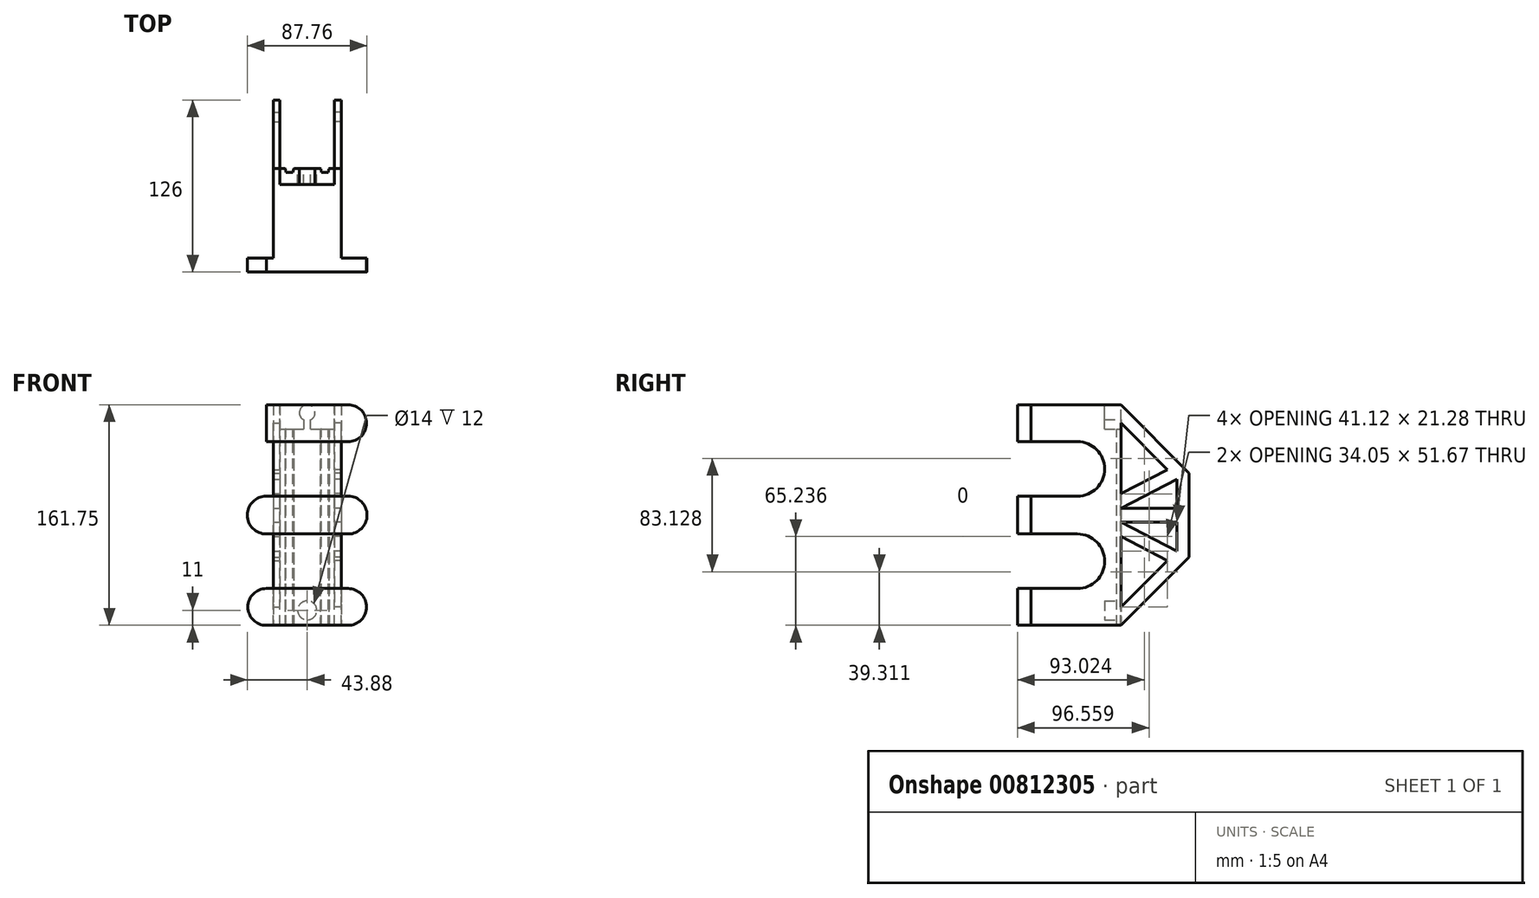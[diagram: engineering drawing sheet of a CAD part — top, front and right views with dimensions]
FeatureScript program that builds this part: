
annotation { "Feature Type Name" : "Feature", "Feature Type Description" : "" }
export const myFeature = defineFeature(function(context is Context, id is Id, definition is map)
    precondition{}
    {
        {
            var Q0;
            Q0=qCreatedBy(makeId("Top.planeOp"),FACE);
            var sketch = newSketch(context, id + "F0", { "sketchPlane" : qUnion([Q0])});
            skLineSegment(sketch, "E0.bottom", {"start": v(-20, 6) * mm, "end": v(20, 6) * mm});
            skLineSegment(sketch, "E0.top", {"start": v(-20, -6) * mm, "end": v(20, -6) * mm});
            skLineSegment(sketch, "E0.left", {"start": v(-20, 6) * mm, "end": v(-20, -6) * mm});
            skLineSegment(sketch, "E0.right", {"start": v(20, 6) * mm, "end": v(20, -6) * mm});
            skLineSegment(sketch, "E1", {"start": v(10.53, 3) * mm, "end": v(15.53, 3) * mm});
            skLineSegment(sketch, "E2", {"start": v(-15.53, 3) * mm, "end": v(-10.53, 3) * mm});
            skLineSegment(sketch, "E3", {"start": v(-20, 6) * mm, "end": v(20, -6) * mm, "construction": true});
            skLineSegment(sketch, "E4", {"start": v(-10.53, 3) * mm, "end": v(-10, 6) * mm});
            skLineSegment(sketch, "E5", {"start": v(-15.53, 3) * mm, "end": v(-16, 6) * mm});
            skLineSegment(sketch, "E6", {"start": v(10.53, 3) * mm, "end": v(10, 6) * mm});
            skLineSegment(sketch, "E7", {"start": v(15.53, 3) * mm, "end": v(16, 6) * mm});
            skSolve(sketch);
        }
        {
            var Q0;
            Q0=qCreatedBy(makeId("Front.planeOp"),FACE);
            var sketch = newSketch(context, id + "F1", { "sketchPlane" : qUnion([Q0])});
            skLineSegment(sketch, "E8", {"start": v(0, 144) * mm, "end": v(0, 0) * mm});
            skSolve(sketch);
        }
        {
            var Q0;
            Q0=makeQuery(id+"F0.imprint","IMPRINT",FACE,{"disambiguationData":[TD([[makeQuery(id+"F0.imprint","IMPRINT",EDGE,{"derivedFrom":sQuery(id+"F0.wireOp",EDGE,"E0.top")}),1.0]])]});
            var Q1;
            Q1=sQuery(id+"F1.wireOp",EDGE,"E8");
            sweep(context, id + "F2", {"profiles" : qUnion([Q0]), "path" : qUnion([Q1])});
        }
        {
            var Q0;
            Q0=makeQuery(id+"F2.opSweep","SWEPT_EDGE",EDGE,{"disambiguationData":[OSD([sQuery(id+"F0.wireOp",EDGE,"E0.bottom"),sQuery(id+"F0.wireOp",EDGE,"E4"),sQuery(id+"F1.wireOp",EDGE,"E8")])]});
            var Q1;
            Q1=makeQuery(id+"F2.opSweep","SWEPT_EDGE",EDGE,{"disambiguationData":[OSD([sQuery(id+"F0.wireOp",EDGE,"E0.bottom"),sQuery(id+"F0.wireOp",EDGE,"E5"),sQuery(id+"F1.wireOp",EDGE,"E8")])]});
            var Q2;
            Q2=makeQuery(id+"F2.opSweep","SWEPT_EDGE",EDGE,{"disambiguationData":[OSD([sQuery(id+"F0.wireOp",EDGE,"E0.bottom"),sQuery(id+"F0.wireOp",EDGE,"E6"),sQuery(id+"F1.wireOp",EDGE,"E8")])]});
            var Q3;
            Q3=makeQuery(id+"F2.opSweep","SWEPT_EDGE",EDGE,{"disambiguationData":[OSD([sQuery(id+"F0.wireOp",EDGE,"E0.bottom"),sQuery(id+"F0.wireOp",EDGE,"E7"),sQuery(id+"F1.wireOp",EDGE,"E8")])]});
            chamfer(context, id + "F3", {"entities" : qUnion([Q0, Q1, Q2, Q3]), "width" : 0.5 * mm, "tangentPropagation" : true});
        }
        {
            var Q0;
            Q0=qCreatedBy(makeId("Front.planeOp"),FACE);
            var sketch = newSketch(context, id + "F4", { "sketchPlane" : qUnion([Q0])});
            skLineSegment(sketch, "E9.0", {"start": v(9.5, 144) * mm, "end": v(-9.5, 144) * mm});
            skLineSegment(sketch, "E10", {"start": v(2.5, 144) * mm, "end": v(2.5, 151) * mm});
            skLineSegment(sketch, "E11", {"start": v(2.5, 151) * mm, "end": v(-2.5, 151) * mm});
            skLineSegment(sketch, "E12", {"start": v(-2.5, 151) * mm, "end": v(-2.5, 144) * mm});
            skLineSegment(sketch, "E13", {"start": v(2.5, 144) * mm, "end": v(9.5, 144) * mm, "construction": true});
            skLineSegment(sketch, "E14", {"start": v(-2.5, 144) * mm, "end": v(-9.5, 144) * mm, "construction": true});
            skPoint(sketch, "E15", {"position": v(0, 156) * mm});
            skCircle(sketch, "E16", {"center": v(0, 156) * mm, "radius": 5.75 * mm});
            skLineSegment(sketch, "E17", {"start": v(0, 144) * mm, "end": v(0, 168) * mm});
            skSolve(sketch);
        }
        {
            var Q0;
            Q0=qCreatedBy(makeId("Front.planeOp"),FACE);
            var sketch = newSketch(context, id + "F5", { "sketchPlane" : qUnion([Q0])});
            skLineSegment(sketch, "E18.0", {"start": v(9.5, 0) * mm, "end": v(-9.5, 0) * mm});
            skLineSegment(sketch, "E19.bottom", {"start": v(3.5, 0) * mm, "end": v(-3.5, 0) * mm});
            skLineSegment(sketch, "E19.top", {"start": v(3.5, 5) * mm, "end": v(-3.5, 5) * mm});
            skLineSegment(sketch, "E19.left", {"start": v(3.5, 0) * mm, "end": v(3.5, 5) * mm});
            skLineSegment(sketch, "E19.right", {"start": v(-3.5, 0) * mm, "end": v(-3.5, 5) * mm});
            skLineSegment(sketch, "E20", {"start": v(9.5, 0) * mm, "end": v(3.5, 0) * mm, "construction": true});
            skLineSegment(sketch, "E21", {"start": v(-3.5, 0) * mm, "end": v(-9.5, 0) * mm, "construction": true});
            skCircle(sketch, "E22", {"center": v(0, 11) * mm, "radius": 7 * mm});
            skPoint(sketch, "E22.centerSnap0", {"position": v(0, 5) * mm});
            skSolve(sketch);
        }
        {
            var Q0;
            {var subQ0=sQuery(id+"F1.wireOp",EDGE,"E8");var subQ1=sQuery(id+"F0.wireOp",EDGE,"E0.bottom");Q0=makeQuery(id+"F2.opSweep","SWEPT_FACE",FACE,{"disambiguationData":[OSD([subQ1,subQ0]),TDD([makeQuery(id+"F0.imprint","IMPRINT",EDGE,{"disambiguationData":[TD([[makeQuery(id+"F0.imprint","INTERSECT",VERTEX,{"derivedFrom":[subQ1,sQuery(id+"F0.wireOp",EDGE,"E4")]}),-1.0]])],"derivedFrom":subQ1}),subQ0])]});}
            var sketch = newSketch(context, id + "F6", { "sketchPlane" : qUnion([Q0])});
            skCircle(sketch, "E23.0", {"center": v(0, 11) * mm, "radius": 7 * mm});
            skLineSegment(sketch, "E24.0", {"start": v(3.5, 0) * mm, "end": v(3.5, 5) * mm});
            skLineSegment(sketch, "E25.0", {"start": v(-3.5, 0) * mm, "end": v(-3.5, 5) * mm});
            skLineSegment(sketch, "E26.0", {"start": v(-3.5, 5) * mm, "end": v(3.5, 5) * mm});
            skLineSegment(sketch, "E27.0", {"start": v(-9.5, 0) * mm, "end": v(9.5, 0) * mm});
            skSolve(sketch);
        }
        {
            var Q0;
            {var subQ5=sQuery(id+"F6.wireOp",EDGE,"E26.0");Q0=makeQuery(id+"F6.imprint","IMPRINT",FACE,{"disambiguationData":[TD([[makeQuery(id+"F6.imprint","IMPRINT",EDGE,{"derivedFrom":subQ5}),1.0]])]});}
            var Q1;
            {var subQ0=sQuery(id+"F6.wireOp",EDGE,"E24.0");var subQ1=sQuery(id+"F6.wireOp",EDGE,"E23.0");var subQ2=makeQuery(id+"F6.imprint","INTERSECT",VERTEX,{"derivedFrom":[subQ1,subQ0]});Q1=makeQuery(id+"F6.imprint","IMPRINT",FACE,{"disambiguationData":[TD([[makeQuery(id+"F6.imprint","IMPRINT",EDGE,{"disambiguationData":[TD([[subQ2,-1.0]])],"derivedFrom":subQ1}),1.0]])]});}
            var Q2;
            {var subQ5=sQuery(id+"F6.wireOp",EDGE,"E26.0");Q2=makeQuery(id+"F6.imprint","IMPRINT",FACE,{"disambiguationData":[TD([[makeQuery(id+"F6.imprint","IMPRINT",EDGE,{"derivedFrom":subQ5}),-1.0]])]});}
            extrude(context, id + "F7", {"entities" : qUnion([Q0, Q1, Q2]), "operationType" : NewBodyOperationType.REMOVE, "oppositeDirection" : true, "depth" : 25.4 * mm, "offsetDistance" : 25.4 * mm});
        }
        {
            var Q0;
            {var subQ0=sQuery(id+"F4.wireOp",EDGE,"E12");var subQ1=sQuery(id+"F4.wireOp",EDGE,"E11");var subQ2=makeQuery(id+"F4.imprint","INTERSECT",VERTEX,{"derivedFrom":[subQ1,subQ0]});Q0=makeQuery(id+"F4.imprint","IMPRINT",FACE,{"disambiguationData":[TD([[makeQuery(id+"F4.imprint","IMPRINT",EDGE,{"disambiguationData":[TD([[subQ2,1.0]])],"derivedFrom":subQ1}),-1.0]])]});}
            var Q1;
            {var subQ0=sQuery(id+"F4.wireOp",EDGE,"E10");var subQ1=sQuery(id+"F4.wireOp",EDGE,"E9.0");var subQ2=makeQuery(id+"F4.imprint","INTERSECT",VERTEX,{"derivedFrom":[subQ1,subQ0]});Q1=makeQuery(id+"F4.imprint","IMPRINT",FACE,{"disambiguationData":[TD([[makeQuery(id+"F4.imprint","IMPRINT",EDGE,{"disambiguationData":[TD([[subQ2,-1.0]])],"derivedFrom":subQ1}),-1.0]])]});}
            var Q2;
            {var subQ0=sQuery(id+"F4.wireOp",EDGE,"E12");var subQ1=sQuery(id+"F4.wireOp",EDGE,"E9.0");var subQ2=makeQuery(id+"F4.imprint","INTERSECT",VERTEX,{"derivedFrom":[subQ1,subQ0]});Q2=makeQuery(id+"F4.imprint","IMPRINT",FACE,{"disambiguationData":[TD([[makeQuery(id+"F4.imprint","IMPRINT",EDGE,{"disambiguationData":[TD([[subQ2,1.0]])],"derivedFrom":subQ1}),-1.0]])]});}
            var Q3;
            {var subQ0=sQuery(id+"F4.wireOp",EDGE,"E12");var subQ1=sQuery(id+"F4.wireOp",EDGE,"E11");var subQ2=makeQuery(id+"F4.imprint","INTERSECT",VERTEX,{"derivedFrom":[subQ1,subQ0]});Q3=makeQuery(id+"F4.imprint","IMPRINT",FACE,{"disambiguationData":[TD([[makeQuery(id+"F4.imprint","IMPRINT",EDGE,{"disambiguationData":[TD([[subQ2,1.0]])],"derivedFrom":subQ1}),1.0]])]});}
            var Q4;
            {var subQ0=sQuery(id+"F4.wireOp",EDGE,"E11");var subQ1=sQuery(id+"F4.wireOp",EDGE,"E10");var subQ2=makeQuery(id+"F4.imprint","INTERSECT",VERTEX,{"derivedFrom":[subQ1,subQ0]});Q4=makeQuery(id+"F4.imprint","IMPRINT",FACE,{"disambiguationData":[TD([[makeQuery(id+"F4.imprint","IMPRINT",EDGE,{"disambiguationData":[TD([[subQ2,1.0]])],"derivedFrom":subQ1}),-1.0]])]});}
            var Q5;
            {var subQ0=sQuery(id+"F4.wireOp",EDGE,"E11");var subQ1=sQuery(id+"F4.wireOp",EDGE,"E10");var subQ2=makeQuery(id+"F4.imprint","INTERSECT",VERTEX,{"derivedFrom":[subQ1,subQ0]});Q5=makeQuery(id+"F4.imprint","IMPRINT",FACE,{"disambiguationData":[TD([[makeQuery(id+"F4.imprint","IMPRINT",EDGE,{"disambiguationData":[TD([[subQ2,1.0]])],"derivedFrom":subQ1}),1.0]])]});}
            extrude(context, id + "F8", {"entities" : qUnion([Q0, Q1, Q2, Q3, Q4, Q5]), "operationType" : NewBodyOperationType.ADD, "endBound" : BoundingType.SYMMETRIC, "depth" : 12 * mm, "offsetDistance" : 25.4 * mm});
        }
        {
            var Q0;
            Q0=qCreatedBy(makeId("Right.planeOp"),FACE);
            var sketch = newSketch(context, id + "F9", { "sketchPlane" : qUnion([Q0])});
            skLineSegment(sketch, "E28.0", {"start": v(-6, 0) * mm, "end": v(-6, 144) * mm});
            skLineSegment(sketch, "E29.0", {"start": v(-6, 150.82) * mm, "end": v(-6, 161.75) * mm});
            skLineSegment(sketch, "E30.0", {"start": v(-6, 144) * mm, "end": v(-6, 150.82) * mm});
            skLineSegment(sketch, "E31", {"start": v(-6, 161.75) * mm, "end": v(-70, 161.75) * mm});
            skLineSegment(sketch, "E32", {"start": v(-70, 0) * mm, "end": v(-6, 0) * mm});
            skLineSegment(sketch, "E33", {"start": v(-70, 161.75) * mm, "end": v(-70, 134.75) * mm});
            skLineSegment(sketch, "E34", {"start": v(-70, 134.75) * mm, "end": v(-6, 134.75) * mm});
            skLineSegment(sketch, "E35", {"start": v(-70, 0) * mm, "end": v(-70, 27) * mm});
            skLineSegment(sketch, "E36", {"start": v(-70, 27) * mm, "end": v(-6, 27) * mm});
            skLineSegment(sketch, "E37", {"start": v(-6, 94.75) * mm, "end": v(-70, 94.75) * mm});
            skLineSegment(sketch, "E38", {"start": v(-70, 67) * mm, "end": v(-6, 67) * mm});
            skLineSegment(sketch, "E39", {"start": v(-70, 94.75) * mm, "end": v(-70, 67) * mm});
            skLineSegment(sketch, "E40.bottom", {"start": v(-70, 161.75) * mm, "end": v(-60, 161.75) * mm});
            skLineSegment(sketch, "E40.top", {"start": v(-70, 134.75) * mm, "end": v(-60, 134.75) * mm});
            skLineSegment(sketch, "E40.right", {"start": v(-60, 161.75) * mm, "end": v(-60, 134.75) * mm});
            skLineSegment(sketch, "E41.bottom", {"start": v(-70, 94.75) * mm, "end": v(-60, 94.75) * mm});
            skLineSegment(sketch, "E41.top", {"start": v(-70, 67) * mm, "end": v(-60, 67) * mm});
            skLineSegment(sketch, "E41.right", {"start": v(-60, 94.75) * mm, "end": v(-60, 67) * mm});
            skLineSegment(sketch, "E42.bottom", {"start": v(-70, 27) * mm, "end": v(-60, 27) * mm});
            skLineSegment(sketch, "E42.top", {"start": v(-70, 0) * mm, "end": v(-60, 0) * mm});
            skLineSegment(sketch, "E42.left", {"start": v(-70, 27) * mm, "end": v(-70, 0) * mm});
            skLineSegment(sketch, "E42.right", {"start": v(-60, 27) * mm, "end": v(-60, 0) * mm});
            skLineSegment(sketch, "E43", {"start": v(-26, 134.75) * mm, "end": v(-26, 94.75) * mm, "construction": true});
            skLineSegment(sketch, "E44", {"start": v(-26, 67) * mm, "end": v(-26, 27) * mm, "construction": true});
            skArc(sketch, "E45", {"start": v(-26, 134.75) * mm, "mid": v(-6, 114.75) * mm, "end": v(-26, 94.75) * mm});
            skArc(sketch, "E46", {"start": v(-26, 67) * mm, "mid": v(-6, 47) * mm, "end": v(-26, 27) * mm});
            skSolve(sketch);
        }
        {
            var Q0;
            {var subQ1=sQuery(id+"F9.wireOp",EDGE,"E29.0");Q0=makeQuery(id+"F9.imprint","IMPRINT",FACE,{"disambiguationData":[TD([[makeQuery(id+"F9.imprint","IMPRINT",EDGE,{"derivedFrom":subQ1}),1.0]])]});}
            var Q1;
            {var subQ0=sQuery(id+"F9.wireOp",EDGE,"E41.right");Q1=makeQuery(id+"F9.imprint","IMPRINT",FACE,{"disambiguationData":[TD([[makeQuery(id+"F9.imprint","IMPRINT",EDGE,{"derivedFrom":subQ0}),1.0]])]});}
            var Q2;
            {var subQ4=sQuery(id+"F9.wireOp",EDGE,"E42.right");Q2=makeQuery(id+"F9.imprint","IMPRINT",FACE,{"disambiguationData":[TD([[makeQuery(id+"F9.imprint","IMPRINT",EDGE,{"derivedFrom":subQ4}),1.0]])]});}
            extrude(context, id + "F10", {"entities" : qUnion([Q0, Q1, Q2]), "operationType" : NewBodyOperationType.ADD, "endBound" : BoundingType.SYMMETRIC, "depth" : 50 * mm, "offsetDistance" : 25.4 * mm});
        }
        {
            var Q0;
            Q0=makeQuery(id+"F2.opSweep","SWEPT_FACE",FACE,{"disambiguationData":[OSD([sQuery(id+"F0.wireOp",EDGE,"E0.right"),sQuery(id+"F1.wireOp",EDGE,"E8")])]});
            var sketch = newSketch(context, id + "F11", { "sketchPlane" : qUnion([Q0])});
            skLineSegment(sketch, "E47", {"start": v(-6, 161.75) * mm, "end": v(6, 161.75) * mm});
            skLineSegment(sketch, "E48.0", {"start": v(-6, 134.75) * mm, "end": v(-6, 161.75) * mm});
            skLineSegment(sketch, "E49.0", {"start": v(-6, 0) * mm, "end": v(6, 0) * mm});
            skLineSegment(sketch, "E50.0", {"start": v(-6, 27) * mm, "end": v(-6, 67) * mm});
            skLineSegment(sketch, "E51.0", {"start": v(-6, 0) * mm, "end": v(-6, 27) * mm});
            skPoint(sketch, "E52.0", {"position": v(-6, 114.75) * mm});
            skLineSegment(sketch, "E53.0", {"start": v(-6, 94.75) * mm, "end": v(-6, 134.75) * mm});
            skLineSegment(sketch, "E54.0", {"start": v(-6, 67) * mm, "end": v(-6, 94.75) * mm});
            skLineSegment(sketch, "E55.0", {"start": v(6, 0) * mm, "end": v(6, 144) * mm});
            skPoint(sketch, "E56.0", {"position": v(6, 147.41) * mm});
            skLineSegment(sketch, "E57.0", {"start": v(6, 150.82) * mm, "end": v(6, 161.75) * mm});
            skLineSegment(sketch, "E58.0", {"start": v(6, 144) * mm, "end": v(6, 150.82) * mm});
            skLineSegment(sketch, "E59", {"start": v(6, 161.75) * mm, "end": v(6, 80.87) * mm, "construction": true});
            skLineSegment(sketch, "E60", {"start": v(6, 80.87) * mm, "end": v(6, 0) * mm, "construction": true});
            skLineSegment(sketch, "E61", {"start": v(6, 80.87) * mm, "end": v(56, 80.87) * mm});
            skLineSegment(sketch, "E62", {"start": v(6, 85.88) * mm, "end": v(56, 85.88) * mm});
            skLineSegment(sketch, "E63", {"start": v(6, 75.87) * mm, "end": v(56, 75.87) * mm});
            skLineSegment(sketch, "E64", {"start": v(56, 111.75) * mm, "end": v(56, 50) * mm});
            skLineSegment(sketch, "E65", {"start": v(6, 161.75) * mm, "end": v(56, 111.75) * mm});
            skLineSegment(sketch, "E66", {"start": v(6, 0) * mm, "end": v(56, 50) * mm});
            skLineSegment(sketch, "E67", {"start": v(56, 111.75) * mm, "end": v(6, 85.88) * mm});
            skLineSegment(sketch, "E68", {"start": v(56, 50) * mm, "end": v(6, 75.87) * mm});
            skLineSegment(sketch, "E69", {"start": v(47.12, 107.15) * mm, "end": v(0, 154.27) * mm});
            skLineSegment(sketch, "E70", {"start": v(47.12, 54.6) * mm, "end": v(0, 7.48) * mm});
            skLineSegment(sketch, "E71", {"start": v(6, 161.75) * mm, "end": v(0, 154.27) * mm});
            skLineSegment(sketch, "E72", {"start": v(6, 0) * mm, "end": v(0, 7.48) * mm});
            skLineSegment(sketch, "E73", {"start": v(40.05, 114.23) * mm, "end": v(-6, 90.4) * mm});
            skLineSegment(sketch, "E74", {"start": v(40.05, 47.52) * mm, "end": v(-6, 71.35) * mm});
            skLineSegment(sketch, "E75", {"start": v(47.12, 107.15) * mm, "end": v(47.12, 54.6) * mm});
            skSolve(sketch);
        }
        {
            var Q0;
            {var subQ1=sQuery(id+"F11.wireOp",EDGE,"E53.0");Q0=makeQuery(id+"F11.imprint","IMPRINT",FACE,{"disambiguationData":[TD([[makeQuery(id+"F11.imprint","IMPRINT",EDGE,{"derivedFrom":subQ1}),-1.0]])]});}
            var Q1;
            {var subQ2=sQuery(id+"F11.wireOp",EDGE,"E57.0");Q1=makeQuery(id+"F11.imprint","IMPRINT",FACE,{"disambiguationData":[TD([[makeQuery(id+"F11.imprint","IMPRINT",EDGE,{"derivedFrom":subQ2}),-1.0]])]});}
            var Q2;
            {var subQ3=sQuery(id+"F11.wireOp",EDGE,"E73");var subQ5=sQuery(id+"F11.wireOp",EDGE,"E69");var subQ7=makeQuery(id+"F11.imprint","INTERSECT",VERTEX,{"derivedFrom":[subQ5,subQ3]});Q2=makeQuery(id+"F11.imprint","IMPRINT",FACE,{"disambiguationData":[TD([[makeQuery(id+"F11.imprint","IMPRINT",EDGE,{"disambiguationData":[TD([[subQ7,-1.0]])],"derivedFrom":subQ3}),1.0]])]});}
            var Q3;
            {var subQ0=sQuery(id+"F11.wireOp",EDGE,"E64");var subQ1=sQuery(id+"F11.wireOp",EDGE,"E62");var subQ2=makeQuery(id+"F11.imprint","INTERSECT",VERTEX,{"derivedFrom":[subQ1,subQ0]});Q3=makeQuery(id+"F11.imprint","IMPRINT",FACE,{"disambiguationData":[TD([[makeQuery(id+"F11.imprint","IMPRINT",EDGE,{"disambiguationData":[TD([[subQ2,1.0]])],"derivedFrom":subQ1}),1.0]])]});}
            var Q4;
            {var subQ0=sQuery(id+"F11.wireOp",EDGE,"E61");var subQ1=sQuery(id+"F11.wireOp",EDGE,"E55.0");var subQ2=makeQuery(id+"F11.imprint","INTERSECT",VERTEX,{"derivedFrom":[subQ1,subQ0]});Q4=makeQuery(id+"F11.imprint","IMPRINT",FACE,{"disambiguationData":[TD([[makeQuery(id+"F11.imprint","IMPRINT",EDGE,{"disambiguationData":[TD([[subQ2,-1.0]])],"derivedFrom":subQ0}),1.0]])]});}
            var Q5;
            {var subQ0=sQuery(id+"F11.wireOp",EDGE,"E64");var subQ1=sQuery(id+"F11.wireOp",EDGE,"E61");var subQ2=makeQuery(id+"F11.imprint","INTERSECT",VERTEX,{"derivedFrom":[subQ1,subQ0]});Q5=makeQuery(id+"F11.imprint","IMPRINT",FACE,{"disambiguationData":[TD([[makeQuery(id+"F11.imprint","IMPRINT",EDGE,{"disambiguationData":[TD([[subQ2,1.0]])],"derivedFrom":subQ1}),1.0]])]});}
            var Q6;
            {var subQ0=sQuery(id+"F11.wireOp",EDGE,"E64");var subQ1=sQuery(id+"F11.wireOp",EDGE,"E61");var subQ2=makeQuery(id+"F11.imprint","INTERSECT",VERTEX,{"derivedFrom":[subQ1,subQ0]});Q6=makeQuery(id+"F11.imprint","IMPRINT",FACE,{"disambiguationData":[TD([[makeQuery(id+"F11.imprint","IMPRINT",EDGE,{"disambiguationData":[TD([[subQ2,1.0]])],"derivedFrom":subQ1}),-1.0]])]});}
            var Q7;
            {var subQ0=sQuery(id+"F11.wireOp",EDGE,"E61");var subQ1=sQuery(id+"F11.wireOp",EDGE,"E55.0");var subQ2=makeQuery(id+"F11.imprint","INTERSECT",VERTEX,{"derivedFrom":[subQ1,subQ0]});Q7=makeQuery(id+"F11.imprint","IMPRINT",FACE,{"disambiguationData":[TD([[makeQuery(id+"F11.imprint","IMPRINT",EDGE,{"disambiguationData":[TD([[subQ2,-1.0]])],"derivedFrom":subQ0}),-1.0]])]});}
            var Q8;
            {var subQ4=sQuery(id+"F11.wireOp",EDGE,"E54.0");var subQ8=sQuery(id+"F11.wireOp",EDGE,"E73");var subQ9=makeQuery(id+"F11.imprint","INTERSECT",VERTEX,{"derivedFrom":[subQ4,subQ8]});Q8=makeQuery(id+"F11.imprint","IMPRINT",FACE,{"disambiguationData":[TD([[makeQuery(id+"F11.imprint","IMPRINT",EDGE,{"disambiguationData":[TD([[subQ9,1.0]])],"derivedFrom":subQ4}),-1.0]])]});}
            var Q9;
            {var subQ3=sQuery(id+"F11.wireOp",EDGE,"E74");var subQ5=sQuery(id+"F11.wireOp",EDGE,"E70");var subQ7=makeQuery(id+"F11.imprint","INTERSECT",VERTEX,{"derivedFrom":[subQ5,subQ3]});Q9=makeQuery(id+"F11.imprint","IMPRINT",FACE,{"disambiguationData":[TD([[makeQuery(id+"F11.imprint","IMPRINT",EDGE,{"disambiguationData":[TD([[subQ7,-1.0]])],"derivedFrom":subQ3}),-1.0]])]});}
            var Q10;
            {var subQ0=sQuery(id+"F11.wireOp",EDGE,"E64");var subQ1=sQuery(id+"F11.wireOp",EDGE,"E63");var subQ2=makeQuery(id+"F11.imprint","INTERSECT",VERTEX,{"derivedFrom":[subQ1,subQ0]});Q10=makeQuery(id+"F11.imprint","IMPRINT",FACE,{"disambiguationData":[TD([[makeQuery(id+"F11.imprint","IMPRINT",EDGE,{"disambiguationData":[TD([[subQ2,1.0]])],"derivedFrom":subQ1}),-1.0]])]});}
            var Q11;
            {var subQ4=sQuery(id+"F11.wireOp",EDGE,"E66");Q11=makeQuery(id+"F11.imprint","IMPRINT",FACE,{"disambiguationData":[TD([[makeQuery(id+"F11.imprint","IMPRINT",EDGE,{"derivedFrom":subQ4}),1.0]])]});}
            var Q12;
            Q12=makeQuery(id+"F11.imprint","IMPRINT",FACE,{"disambiguationData":[TD([[makeQuery(id+"F11.imprint","IMPRINT",EDGE,{"derivedFrom":sQuery(id+"F11.wireOp",EDGE,"E49.0")}),1.0]])]});
            var Q13;
            {var subQ0=sQuery(id+"F11.wireOp",EDGE,"E72");Q13=makeQuery(id+"F11.imprint","IMPRINT",FACE,{"disambiguationData":[TD([[makeQuery(id+"F11.imprint","IMPRINT",EDGE,{"derivedFrom":subQ0}),-1.0]])]});}
            var Q14;
            {var subQ0=sQuery(id+"F11.wireOp",EDGE,"E57.0");Q14=makeQuery(id+"F11.imprint","IMPRINT",FACE,{"disambiguationData":[TD([[makeQuery(id+"F11.imprint","IMPRINT",EDGE,{"derivedFrom":subQ0}),1.0]])]});}
            var Q15;
            {var subQ6=sQuery(id+"F11.wireOp",EDGE,"E47");Q15=makeQuery(id+"F11.imprint","IMPRINT",FACE,{"disambiguationData":[TD([[makeQuery(id+"F11.imprint","IMPRINT",EDGE,{"derivedFrom":subQ6}),-1.0]])]});}
            extrude(context, id + "F12", {"entities" : qUnion([Q0, Q1, Q2, Q3, Q4, Q5, Q6, Q7, Q8, Q9, Q10, Q11, Q12, Q13, Q14, Q15]), "operationType" : NewBodyOperationType.ADD, "depth" : 5 * mm, "offsetDistance" : 25.4 * mm});
        }
        {
            var Q0;
            Q0=makeQuery(id+"F2.opSweep","SWEPT_BODY",BODY,{"disambiguationData":[OSD([sQuery(id+"F0.wireOp",EDGE,"E0.bottom"),sQuery(id+"F0.wireOp",EDGE,"E0.top"),sQuery(id+"F0.wireOp",EDGE,"E0.left"),sQuery(id+"F0.wireOp",EDGE,"E0.right"),sQuery(id+"F0.wireOp",EDGE,"E1"),sQuery(id+"F0.wireOp",EDGE,"E2"),sQuery(id+"F0.wireOp",EDGE,"E4"),sQuery(id+"F0.wireOp",EDGE,"E5"),sQuery(id+"F0.wireOp",EDGE,"E6"),sQuery(id+"F0.wireOp",EDGE,"E7"),sQuery(id+"F1.wireOp",EDGE,"E8")])]});
            var Q1;
            {var subQ0=sQuery(id+"F9.wireOp",EDGE,"E28.0");Q1=makeQuery(id+"F12.boolean.opBoolean","MERGE",FACE,{"derivedFrom":[makeQuery(id+"F10.opExtrude","CAP_FACE",FACE,{"disambiguationData":[OSD([subQ0,sQuery(id+"F9.wireOp",EDGE,"E37"),sQuery(id+"F9.wireOp",EDGE,"E38"),sQuery(id+"F9.wireOp",EDGE,"E41.right")])],"isStart":false}),makeQuery(id+"F10.opExtrude","CAP_FACE",FACE,{"disambiguationData":[OSD([subQ0,sQuery(id+"F9.wireOp",EDGE,"E32"),sQuery(id+"F9.wireOp",EDGE,"E36"),sQuery(id+"F9.wireOp",EDGE,"E42.right")])],"isStart":false}),makeQuery(id+"F10.opExtrude","CAP_FACE",FACE,{"disambiguationData":[OSD([subQ0,sQuery(id+"F9.wireOp",EDGE,"E29.0"),sQuery(id+"F9.wireOp",EDGE,"E30.0"),sQuery(id+"F9.wireOp",EDGE,"E31"),sQuery(id+"F9.wireOp",EDGE,"E34"),sQuery(id+"F9.wireOp",EDGE,"E40.right")])],"isStart":false}),makeQuery(id+"F12.opExtrude","CAP_FACE",FACE,{"disambiguationData":[OSD([sQuery(id+"F11.wireOp",EDGE,"E47"),sQuery(id+"F11.wireOp",EDGE,"E48.0"),sQuery(id+"F11.wireOp",EDGE,"E49.0"),sQuery(id+"F11.wireOp",EDGE,"E50.0"),sQuery(id+"F11.wireOp",EDGE,"E51.0"),sQuery(id+"F11.wireOp",EDGE,"E53.0"),sQuery(id+"F11.wireOp",EDGE,"E54.0"),sQuery(id+"F11.wireOp",EDGE,"E55.0"),sQuery(id+"F11.wireOp",EDGE,"E58.0"),sQuery(id+"F11.wireOp",EDGE,"E62"),sQuery(id+"F11.wireOp",EDGE,"E63"),sQuery(id+"F11.wireOp",EDGE,"E64"),sQuery(id+"F11.wireOp",EDGE,"E65"),sQuery(id+"F11.wireOp",EDGE,"E66"),sQuery(id+"F11.wireOp",EDGE,"E67"),sQuery(id+"F11.wireOp",EDGE,"E68"),sQuery(id+"F11.wireOp",EDGE,"E69"),sQuery(id+"F11.wireOp",EDGE,"E70"),sQuery(id+"F11.wireOp",EDGE,"E73"),sQuery(id+"F11.wireOp",EDGE,"E74"),sQuery(id+"F11.wireOp",EDGE,"E75")])],"isStart":false})]});}
            var Q2;
            Q2=qCreatedBy(makeId("Right.planeOp"),FACE);
            mirror(context, id + "F13", {"operationType" : NewBodyOperationType.ADD, "entities" : qUnion([Q0]), "faces" : qUnion([Q1]), "mirrorPlane" : qUnion([Q2])});
        }
        {
            var Q0;
            {var subQ0=sQuery(id+"F9.wireOp",EDGE,"E45");var subQ1=sQuery(id+"F9.wireOp",EDGE,"E28.0");var subQ2=makeQuery(id+"F9.imprint","INTERSECT",VERTEX,{"derivedFrom":[subQ1,subQ0]});Q0=makeQuery(id+"F9.imprint","IMPRINT",FACE,{"disambiguationData":[TD([[makeQuery(id+"F9.imprint","IMPRINT",EDGE,{"disambiguationData":[TD([[subQ2,-1.0]])],"derivedFrom":subQ1}),1.0]])]});}
            var Q1;
            {var subQ0=sQuery(id+"F9.wireOp",EDGE,"E37");var subQ1=sQuery(id+"F9.wireOp",EDGE,"E28.0");var subQ2=makeQuery(id+"F9.imprint","INTERSECT",VERTEX,{"derivedFrom":[subQ1,subQ0]});Q1=makeQuery(id+"F9.imprint","IMPRINT",FACE,{"disambiguationData":[TD([[makeQuery(id+"F9.imprint","IMPRINT",EDGE,{"disambiguationData":[TD([[subQ2,-1.0]])],"derivedFrom":subQ1}),1.0]])]});}
            var Q2;
            {var subQ0=sQuery(id+"F9.wireOp",EDGE,"E36");var subQ1=sQuery(id+"F9.wireOp",EDGE,"E28.0");var subQ2=makeQuery(id+"F9.imprint","INTERSECT",VERTEX,{"derivedFrom":[subQ1,subQ0]});Q2=makeQuery(id+"F9.imprint","IMPRINT",FACE,{"disambiguationData":[TD([[makeQuery(id+"F9.imprint","IMPRINT",EDGE,{"disambiguationData":[TD([[subQ2,-1.0]])],"derivedFrom":subQ1}),1.0]])]});}
            var Q3;
            {var subQ0=sQuery(id+"F9.wireOp",EDGE,"E38");var subQ1=sQuery(id+"F9.wireOp",EDGE,"E28.0");var subQ2=makeQuery(id+"F9.imprint","INTERSECT",VERTEX,{"derivedFrom":[subQ1,subQ0]});Q3=makeQuery(id+"F9.imprint","IMPRINT",FACE,{"disambiguationData":[TD([[makeQuery(id+"F9.imprint","IMPRINT",EDGE,{"disambiguationData":[TD([[subQ2,1.0]])],"derivedFrom":subQ1}),1.0]])]});}
            extrude(context, id + "F14", {"entities" : qUnion([Q0, Q1, Q2, Q3]), "operationType" : NewBodyOperationType.ADD, "endBound" : BoundingType.SYMMETRIC, "depth" : 50 * mm, "offsetDistance" : 25.4 * mm});
        }
        {
            var Q0;
            {var subQ2=sQuery(id+"F9.wireOp",EDGE,"E35");Q0=makeQuery(id+"F9.imprint","IMPRINT",FACE,{"disambiguationData":[TD([[makeQuery(id+"F9.imprint","IMPRINT",EDGE,{"derivedFrom":subQ2}),-1.0]])]});}
            var Q1;
            {var subQ0=sQuery(id+"F9.wireOp",EDGE,"E39");Q1=makeQuery(id+"F9.imprint","IMPRINT",FACE,{"disambiguationData":[TD([[makeQuery(id+"F9.imprint","IMPRINT",EDGE,{"derivedFrom":subQ0}),1.0]])]});}
            var Q2;
            {var subQ0=sQuery(id+"F9.wireOp",EDGE,"E33");Q2=makeQuery(id+"F9.imprint","IMPRINT",FACE,{"disambiguationData":[TD([[makeQuery(id+"F9.imprint","IMPRINT",EDGE,{"derivedFrom":subQ0}),1.0]])]});}
            extrude(context, id + "F15", {"entities" : qUnion([Q0, Q1, Q2]), "operationType" : NewBodyOperationType.ADD, "endBound" : BoundingType.SYMMETRIC, "depth" : 60 * mm, "offsetDistance" : 25.4 * mm});
        }
        {
            var Q0;
            {var subQ0=sQuery(id+"F9.wireOp",EDGE,"E45");var subQ1=sQuery(id+"F9.wireOp",EDGE,"E37");var subQ2=sQuery(id+"F9.wireOp",EDGE,"E28.0");var subQ7=sQuery(id+"F9.wireOp",EDGE,"E40.right");Q0=makeQuery(id+"F15.boolean.opBoolean","SPLIT",FACE,{"disambiguationData":[TD([makeQuery(id+"F14.opExtrude","CAP_FACE",FACE,{"disambiguationData":[OSD([subQ2,subQ1,subQ0])],"isStart":true})])],"derivedFrom":makeQuery(id+"F15.opExtrude","SWEPT_FACE",FACE,{"disambiguationData":[OSD([subQ7])]})});}
            var sketch = newSketch(context, id + "F16", { "sketchPlane" : qUnion([Q0])});
            skArc(sketch, "E76", {"start": v(30, 161.75) * mm, "mid": v(43.5, 148.25) * mm, "end": v(30, 134.75) * mm});
            skLineSegment(sketch, "E77.0", {"start": v(30, 161.75) * mm, "end": v(30, 134.75) * mm});
            skLineSegment(sketch, "E78.0", {"start": v(-30, 161.75) * mm, "end": v(-30, 134.75) * mm});
            skLineSegment(sketch, "E79.0", {"start": v(-30, 94.75) * mm, "end": v(-30, 67) * mm});
            skLineSegment(sketch, "E80.0", {"start": v(30, 94.75) * mm, "end": v(30, 67) * mm});
            skLineSegment(sketch, "E81.0", {"start": v(-30, 27) * mm, "end": v(-30, 0) * mm});
            skLineSegment(sketch, "E82.0", {"start": v(30, 27) * mm, "end": v(30, 0) * mm});
            skArc(sketch, "E83", {"start": v(-30, 161.75) * mm, "mid": v(-43.5, 148.25) * mm, "end": v(-30, 134.75) * mm});
            skArc(sketch, "E84", {"start": v(-30, 94.75) * mm, "mid": v(-43.87, 80.87) * mm, "end": v(-30, 67) * mm});
            skArc(sketch, "E85", {"start": v(30, 94.75) * mm, "mid": v(43.87, 80.87) * mm, "end": v(30, 67) * mm});
            skArc(sketch, "E86", {"start": v(30, 27) * mm, "mid": v(43.5, 13.5) * mm, "end": v(30, 0) * mm});
            skArc(sketch, "E87", {"start": v(-30, 27) * mm, "mid": v(-43.5, 13.5) * mm, "end": v(-30, 0) * mm});
            skSolve(sketch);
        }
        {
            var Q0;
            Q0=makeQuery(id+"F16.imprint","IMPRINT",FACE,{"disambiguationData":[TD([[makeQuery(id+"F16.imprint","IMPRINT",EDGE,{"derivedFrom":sQuery(id+"F16.wireOp",EDGE,"E81.0")}),-1.0]])]});
            var Q1;
            Q1=makeQuery(id+"F16.imprint","IMPRINT",FACE,{"disambiguationData":[TD([[makeQuery(id+"F16.imprint","IMPRINT",EDGE,{"derivedFrom":sQuery(id+"F16.wireOp",EDGE,"E79.0")}),-1.0]])]});
            var Q2;
            Q2=makeQuery(id+"F16.imprint","IMPRINT",FACE,{"disambiguationData":[TD([[makeQuery(id+"F16.imprint","IMPRINT",EDGE,{"derivedFrom":sQuery(id+"F16.wireOp",EDGE,"E78.0")}),-1.0]])]});
            var Q3;
            Q3=makeQuery(id+"F16.imprint","IMPRINT",FACE,{"disambiguationData":[TD([[makeQuery(id+"F16.imprint","IMPRINT",EDGE,{"derivedFrom":sQuery(id+"F16.wireOp",EDGE,"E76")}),-1.0]])]});
            var Q4;
            Q4=makeQuery(id+"F16.imprint","IMPRINT",FACE,{"disambiguationData":[TD([[makeQuery(id+"F16.imprint","IMPRINT",EDGE,{"derivedFrom":sQuery(id+"F16.wireOp",EDGE,"E80.0")}),1.0]])]});
            var Q5;
            Q5=makeQuery(id+"F16.imprint","IMPRINT",FACE,{"disambiguationData":[TD([[makeQuery(id+"F16.imprint","IMPRINT",EDGE,{"derivedFrom":sQuery(id+"F16.wireOp",EDGE,"E82.0")}),1.0]])]});
            extrude(context, id + "F17", {"entities" : qUnion([Q0, Q1, Q2, Q3, Q4, Q5]), "operationType" : NewBodyOperationType.ADD, "oppositeDirection" : true, "depth" : 10 * mm, "offsetDistance" : 25.4 * mm});
        }
    });
